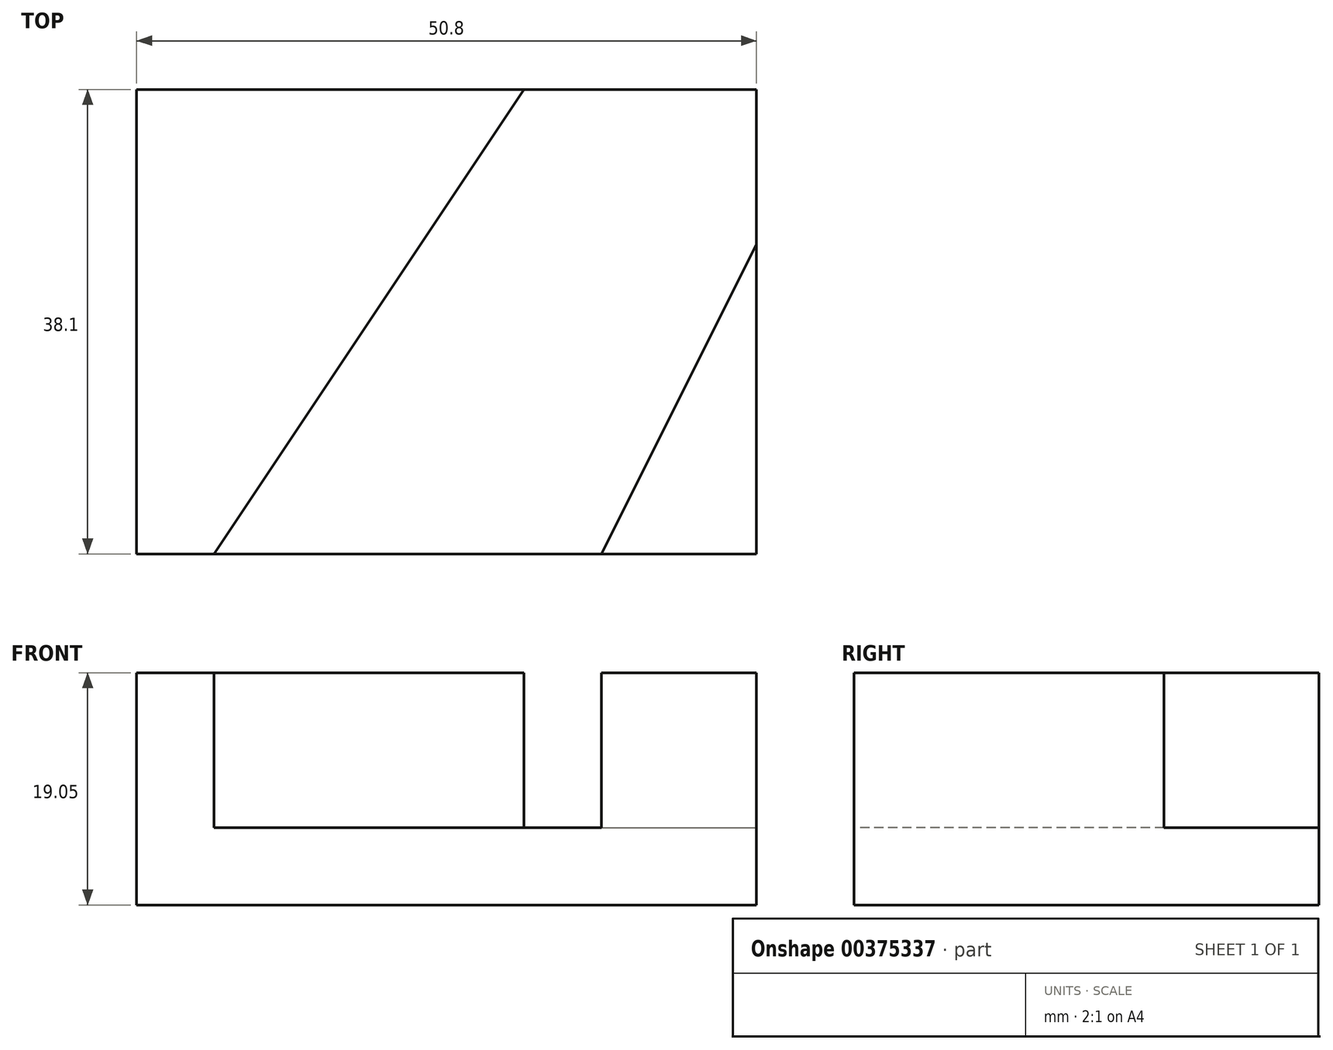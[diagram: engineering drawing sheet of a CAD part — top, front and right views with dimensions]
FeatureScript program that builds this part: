
annotation { "Feature Type Name" : "Feature", "Feature Type Description" : "" }
export const myFeature = defineFeature(function(context is Context, id is Id, definition is map)
    precondition{}
    {
        {
            var Q0;
            Q0=qCreatedBy(makeId("Front.planeOp"),FACE);
            var sketch = newSketch(context, id + "F0", { "sketchPlane" : qUnion([Q0])});
            skLineSegment(sketch, "E0", {"start": v(0, 0) * mm, "end": v(-50.8, 0) * mm});
            skLineSegment(sketch, "E1", {"start": v(-50.8, 0) * mm, "end": v(-50.8, 19.05) * mm});
            skLineSegment(sketch, "E2", {"start": v(0, 0) * mm, "end": v(0, 19.05) * mm});
            skLineSegment(sketch, "E3", {"start": v(-50.8, 19.05) * mm, "end": v(-44.45, 19.05) * mm});
            skLineSegment(sketch, "E4", {"start": v(0, 19.05) * mm, "end": v(-12.7, 19.05) * mm});
            skLineSegment(sketch, "E5", {"start": v(-44.45, 19.05) * mm, "end": v(-44.45, 6.35) * mm});
            skLineSegment(sketch, "E6", {"start": v(-12.7, 19.05) * mm, "end": v(-12.7, 6.35) * mm});
            skLineSegment(sketch, "E7", {"start": v(-44.45, 6.35) * mm, "end": v(-12.7, 6.35) * mm});
            skSolve(sketch);
        }
        {
            var Q0;
            Q0 = qSketchRegion(id + "F0", true);
            extrude(context, id + "F1", {"entities" : qUnion([Q0]), "depth" : 38.1 * mm});
        }
        {
            var Q0;
            Q0=makeQuery(id+"F1.opExtrude","SWEPT_FACE",FACE,{"disambiguationData":[OSD([sQuery(id+"F0.wireOp",EDGE,"E4")])]});
            var sketch = newSketch(context, id + "F2", { "sketchPlane" : qUnion([Q0])});
            skLineSegment(sketch, "E8", {"start": v(0, -38.1) * mm, "end": v(0, -12.7) * mm});
            skLineSegment(sketch, "E9", {"start": v(-12.7, -38.1) * mm, "end": v(0, -12.7) * mm});
            skSolve(sketch);
        }
        {
            var Q0;
            Q0 = qSketchRegion(id + "F2", true);
            var Q1;
            {var subQ0=sQuery(id+"F2.wireOp",EDGE,"E9");Q1=makeQuery(id+"F2.imprint","IMPRINT",FACE,{"disambiguationData":[TD([[makeQuery(id+"F2.imprint","IMPRINT",EDGE,{"derivedFrom":subQ0}),1.0]])]});}
            extrude(context, id + "F3", {"entities" : qUnion([Q0, Q1]), "operationType" : NewBodyOperationType.REMOVE, "oppositeDirection" : true, "depth" : 12.7 * mm});
        }
        {
            var Q0;
            Q0=makeQuery(id+"F3.boolean.opBoolean","MERGE",FACE,{"derivedFrom":[makeQuery(id+"F1.opExtrude","SWEPT_FACE",FACE,{"disambiguationData":[OSD([sQuery(id+"F0.wireOp",EDGE,"E7")])]}),makeQuery(id+"F3.opExtrude","CAP_FACE",FACE,{"disambiguationData":[OSD([sQuery(id+"F0.wireOp",EDGE,"E2"),sQuery(id+"F0.wireOp",EDGE,"E4"),sQuery(id+"F0.wireOp",EDGE,"E6"),sQuery(id+"F2.wireOp",EDGE,"E9")])],"isStart":false})]});
            var sketch = newSketch(context, id + "F4", { "sketchPlane" : qUnion([Q0])});
            skLineSegment(sketch, "E10", {"start": v(-44.45, 0) * mm, "end": v(-19.05, 0) * mm});
            skLineSegment(sketch, "E11", {"start": v(-19.05, 0) * mm, "end": v(-44.45, -38.1) * mm});
            skSolve(sketch);
        }
        {
            var Q0;
            Q0 = qSketchRegion(id + "F4", true);
            var Q1;
            Q1=makeQuery(id+"F4.imprint","IMPRINT",FACE,{"disambiguationData":[TD([[makeQuery(id+"F4.imprint","IMPRINT",EDGE,{"derivedFrom":sQuery(id+"F4.wireOp",EDGE,"E10")}),-1.0]])]});
            extrude(context, id + "F5", {"entities" : qUnion([Q0, Q1]), "operationType" : NewBodyOperationType.ADD, "depth" : 12.7 * mm});
        }
    });
